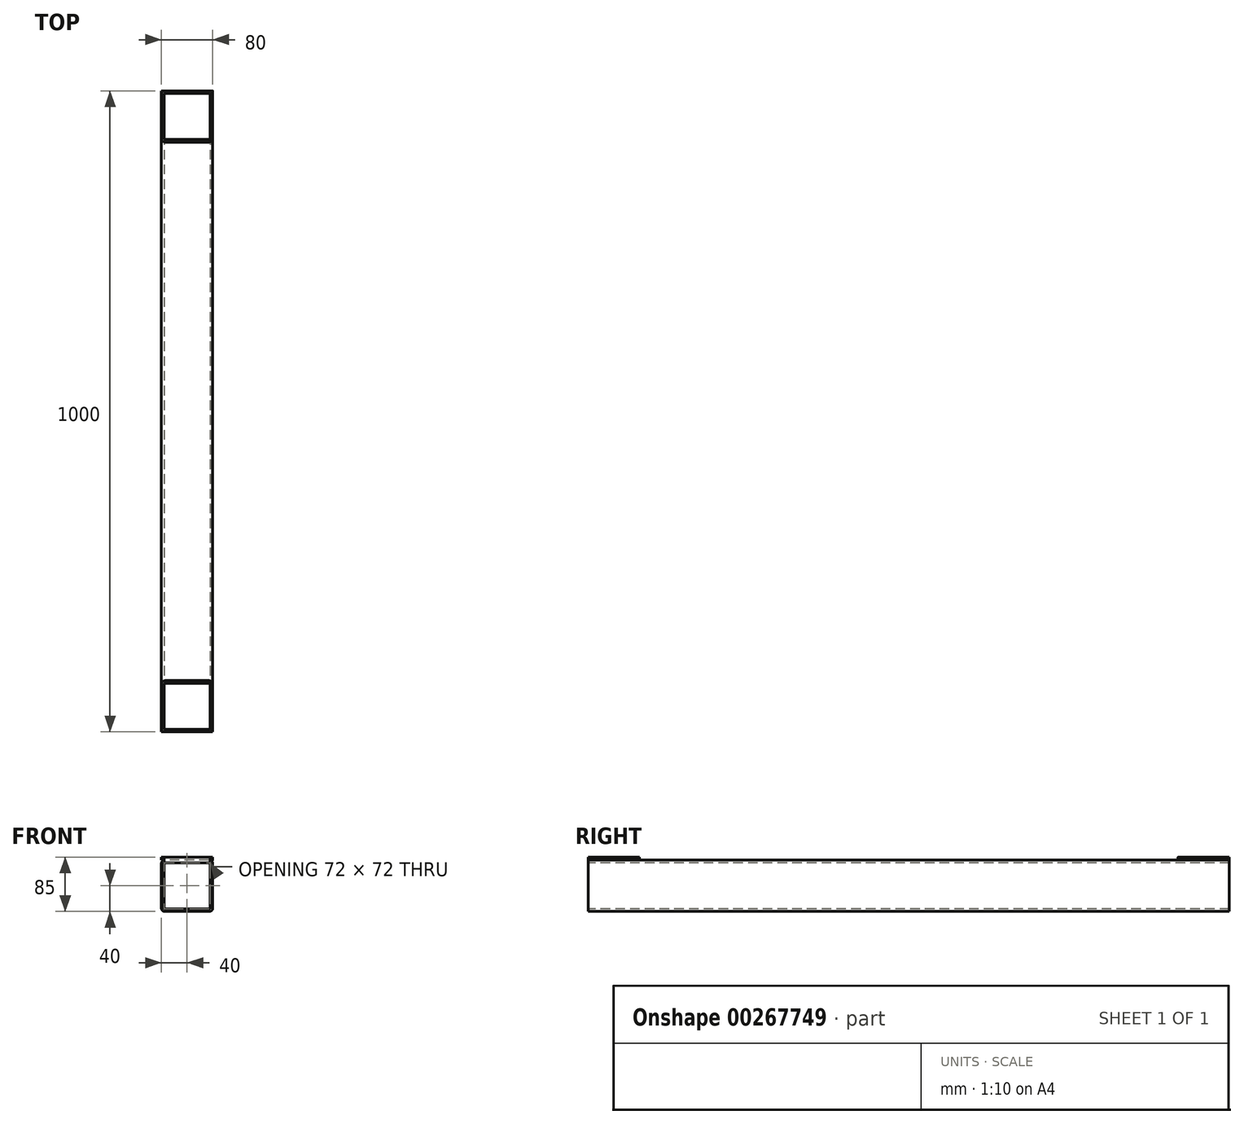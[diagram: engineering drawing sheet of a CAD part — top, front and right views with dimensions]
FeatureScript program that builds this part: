
annotation { "Feature Type Name" : "Feature", "Feature Type Description" : "" }
export const myFeature = defineFeature(function(context is Context, id is Id, definition is map)
    precondition{}
    {
        {
            var Q0;
            Q0=qCreatedBy(makeId("Front.planeOp"),FACE);
            var sketch = newSketch(context, id + "F0", { "sketchPlane" : qUnion([Q0])});
            skLineSegment(sketch, "E0.bottom", {"start": v(35, 40) * mm, "end": v(-35, 40) * mm});
            skLineSegment(sketch, "E0.top", {"start": v(35, -40) * mm, "end": v(-35, -40) * mm});
            skLineSegment(sketch, "E0.left", {"start": v(40, 35) * mm, "end": v(40, -35) * mm});
            skLineSegment(sketch, "E0.right", {"start": v(-40, 35) * mm, "end": v(-40, -35) * mm});
            skPoint(sketch, "E0.middle", {"position": v(0, 0) * mm});
            skPoint(sketch, "E1.visualSharp", {"position": v(-40, 40) * mm});
            skArc(sketch, "E1.filletArc", {"start": v(-35, 40) * mm, "mid": v(-38.54, 38.54) * mm, "end": v(-40, 35) * mm});
            skPoint(sketch, "E2.visualSharp", {"position": v(40, 40) * mm});
            skArc(sketch, "E2.filletArc", {"start": v(40, 35) * mm, "mid": v(38.54, 38.54) * mm, "end": v(35, 40) * mm});
            skPoint(sketch, "E3.visualSharp", {"position": v(40, -40) * mm});
            skArc(sketch, "E3.filletArc", {"start": v(35, -40) * mm, "mid": v(38.54, -38.54) * mm, "end": v(40, -35) * mm});
            skPoint(sketch, "E4.visualSharp", {"position": v(-40, -40) * mm});
            skArc(sketch, "E4.filletArc", {"start": v(-40, -35) * mm, "mid": v(-38.54, -38.54) * mm, "end": v(-35, -40) * mm});
            skArc(sketch, "E5.0", {"start": v(-35, 36) * mm, "mid": v(-35.7, 35.7) * mm, "end": v(-36, 35) * mm});
            skLineSegment(sketch, "E5.1", {"start": v(35, 36) * mm, "end": v(-35, 36) * mm});
            skLineSegment(sketch, "E5.2", {"start": v(-36, 35) * mm, "end": v(-36, -35) * mm});
            skArc(sketch, "E5.3", {"start": v(36, 35) * mm, "mid": v(35.7, 35.7) * mm, "end": v(35, 36) * mm});
            skArc(sketch, "E5.4", {"start": v(-36, -35) * mm, "mid": v(-35.7, -35.7) * mm, "end": v(-35, -36) * mm});
            skLineSegment(sketch, "E5.5", {"start": v(35, -36) * mm, "end": v(-35, -36) * mm});
            skArc(sketch, "E5.6", {"start": v(35, -36) * mm, "mid": v(35.7, -35.7) * mm, "end": v(36, -35) * mm});
            skLineSegment(sketch, "E5.7", {"start": v(36, 35) * mm, "end": v(36, -35) * mm});
            skSolve(sketch);
        }
        {
            var Q0;
            Q0=makeQuery(id+"F0.imprint","IMPRINT",FACE,{"disambiguationData":[TD([[makeQuery(id+"F0.imprint","IMPRINT",EDGE,{"derivedFrom":sQuery(id+"F0.wireOp",EDGE,"E0.bottom")}),1.0]])]});
            extrude(context, id + "F1", {"entities" : qUnion([Q0]), "oppositeDirection" : true, "depth" : 1000 * mm});
        }
        {
            var Q0;
            Q0=makeQuery(id+"F1.opExtrude","SWEPT_FACE",FACE,{"disambiguationData":[OSD([sQuery(id+"F0.wireOp",EDGE,"E0.bottom")])]});
            var sketch = newSketch(context, id + "F2", { "sketchPlane" : qUnion([Q0])});
            skLineSegment(sketch, "E6.bottom", {"start": v(34, 80) * mm, "end": v(-34, 80) * mm});
            skLineSegment(sketch, "E6.top", {"start": v(34, 0) * mm, "end": v(-34, 0) * mm});
            skLineSegment(sketch, "E6.left", {"start": v(40, 74) * mm, "end": v(40, 6) * mm});
            skLineSegment(sketch, "E6.right", {"start": v(-40, 74) * mm, "end": v(-40, 6) * mm});
            skPoint(sketch, "E6.middle", {"position": v(0, 40) * mm});
            skPoint(sketch, "E7.visualSharp", {"position": v(-40, 80) * mm});
            skArc(sketch, "E7.filletArc", {"start": v(-34, 80) * mm, "mid": v(-38.24, 78.24) * mm, "end": v(-40, 74) * mm});
            skPoint(sketch, "E8.visualSharp", {"position": v(-40, 0) * mm});
            skArc(sketch, "E8.filletArc", {"start": v(-40, 6) * mm, "mid": v(-38.24, 1.76) * mm, "end": v(-34, 0) * mm});
            skPoint(sketch, "E9.visualSharp", {"position": v(40, 0) * mm});
            skArc(sketch, "E9.filletArc", {"start": v(34, 0) * mm, "mid": v(38.24, 1.76) * mm, "end": v(40, 6) * mm});
            skPoint(sketch, "E10.visualSharp", {"position": v(40, 80) * mm});
            skArc(sketch, "E10.filletArc", {"start": v(40, 74) * mm, "mid": v(38.24, 78.24) * mm, "end": v(34, 80) * mm});
            skLineSegment(sketch, "E11.0", {"start": v(36, 74) * mm, "end": v(36, 6) * mm});
            skArc(sketch, "E11.1", {"start": v(34, 4) * mm, "mid": v(35.41, 4.59) * mm, "end": v(36, 6) * mm});
            skArc(sketch, "E11.2", {"start": v(36, 74) * mm, "mid": v(35.41, 75.41) * mm, "end": v(34, 76) * mm});
            skLineSegment(sketch, "E11.3", {"start": v(34, 4) * mm, "end": v(-34, 4) * mm});
            skLineSegment(sketch, "E11.4", {"start": v(34, 76) * mm, "end": v(-34, 76) * mm});
            skArc(sketch, "E11.5", {"start": v(-34, 76) * mm, "mid": v(-35.41, 75.41) * mm, "end": v(-36, 74) * mm});
            skLineSegment(sketch, "E11.6", {"start": v(-36, 74) * mm, "end": v(-36, 6) * mm});
            skArc(sketch, "E11.7", {"start": v(-36, 6) * mm, "mid": v(-35.41, 4.59) * mm, "end": v(-34, 4) * mm});
            skSolve(sketch);
        }
        {
            var Q0;
            Q0 = qSketchRegion(id + "F2", true);
            extrude(context, id + "F3", {"entities" : qUnion([Q0]), "operationType" : NewBodyOperationType.ADD, "depth" : 5 * mm});
        }
        {
            var Q0;
            {var subQ0=sQuery(id+"F2.wireOp",EDGE,"E6.bottom");var subQ3=sQuery(id+"F0.wireOp",EDGE,"E0.bottom");Q0=makeQuery(id+"F3.boolean.opBoolean","SPLIT",FACE,{"disambiguationData":[TD([makeQuery(id+"F3.opExtrude","SWEPT_FACE",FACE,{"disambiguationData":[OSD([subQ0])]})])],"derivedFrom":makeQuery(id+"F1.opExtrude","SWEPT_FACE",FACE,{"disambiguationData":[OSD([subQ3])]})});}
            var sketch = newSketch(context, id + "F4", { "sketchPlane" : qUnion([Q0])});
            skLineSegment(sketch, "E12.bottom", {"start": v(34, 1000) * mm, "end": v(-34, 1000) * mm});
            skLineSegment(sketch, "E12.top", {"start": v(34, 920) * mm, "end": v(-34, 920) * mm});
            skLineSegment(sketch, "E12.left", {"start": v(40, 994) * mm, "end": v(40, 926) * mm});
            skLineSegment(sketch, "E12.right", {"start": v(-40, 994) * mm, "end": v(-40, 926) * mm});
            skPoint(sketch, "E12.middle", {"position": v(0, 960) * mm});
            skPoint(sketch, "E13.visualSharp", {"position": v(-40, 1000) * mm});
            skArc(sketch, "E13.filletArc", {"start": v(-34, 1000) * mm, "mid": v(-38.24, 998.24) * mm, "end": v(-40, 994) * mm});
            skPoint(sketch, "E14.visualSharp", {"position": v(-40, 920) * mm});
            skArc(sketch, "E14.filletArc", {"start": v(-40, 926) * mm, "mid": v(-38.24, 921.76) * mm, "end": v(-34, 920) * mm});
            skPoint(sketch, "E15.visualSharp", {"position": v(40, 920) * mm});
            skArc(sketch, "E15.filletArc", {"start": v(34, 920) * mm, "mid": v(38.24, 921.76) * mm, "end": v(40, 926) * mm});
            skPoint(sketch, "E16.visualSharp", {"position": v(40, 1000) * mm});
            skArc(sketch, "E16.filletArc", {"start": v(40, 994) * mm, "mid": v(38.24, 998.24) * mm, "end": v(34, 1000) * mm});
            skLineSegment(sketch, "E17.0", {"start": v(36, 994) * mm, "end": v(36, 926) * mm});
            skArc(sketch, "E17.1", {"start": v(34, 924) * mm, "mid": v(35.41, 924.59) * mm, "end": v(36, 926) * mm});
            skArc(sketch, "E17.2", {"start": v(36, 994) * mm, "mid": v(35.41, 995.41) * mm, "end": v(34, 996) * mm});
            skLineSegment(sketch, "E17.3", {"start": v(34, 924) * mm, "end": v(-34, 924) * mm});
            skLineSegment(sketch, "E17.4", {"start": v(34, 996) * mm, "end": v(-34, 996) * mm});
            skArc(sketch, "E17.5", {"start": v(-34, 996) * mm, "mid": v(-35.41, 995.41) * mm, "end": v(-36, 994) * mm});
            skLineSegment(sketch, "E17.6", {"start": v(-36, 994) * mm, "end": v(-36, 926) * mm});
            skArc(sketch, "E17.7", {"start": v(-36, 926) * mm, "mid": v(-35.41, 924.59) * mm, "end": v(-34, 924) * mm});
            skSolve(sketch);
        }
        {
            var Q0;
            Q0 = qSketchRegion(id + "F4", true);
            extrude(context, id + "F5", {"entities" : qUnion([Q0]), "operationType" : NewBodyOperationType.ADD, "depth" : 5 * mm});
        }
    });
